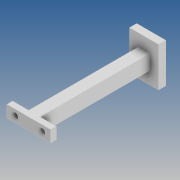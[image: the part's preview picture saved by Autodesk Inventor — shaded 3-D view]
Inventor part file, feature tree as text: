
AUTODESK INVENTOR PART (.ipt)
format: ipt  version: 2020 (Build 240168000, 168)  size: 304,128 bytes
history: native  units: mm
features: sketch x5, extrude x4, other x1, hole x1
ambient origin geometry x8: Origin, YZ Plane, XZ Plane, XY Plane, X Axis, Y Axis, Z Axis, Center Point
bodies: Body1 (feature_tree)
feature tree (11):
  other  "솔리드1"
  extrude  "돌출1"  Depth=20.0mm
  extrude  "돌출2"  Depth=27.0mm
  extrude  "돌출11"  Depth=5.0mm TaperAngle=0.0deg
  hole  "구멍2"  [1 undecoded]
  extrude  "돌출12"  Depth=10.0mm
  sketch  "스케치1"
  sketch  "스케치2"
  sketch  "스케치3"
  sketch  "스케치9"
  sketch  "스케치10"
note: 1 required parameter value undecoded (feature->parameter linkage not recoverable at this tier; creation-order binding heuristic only, values carry confidence <= 0.55)
